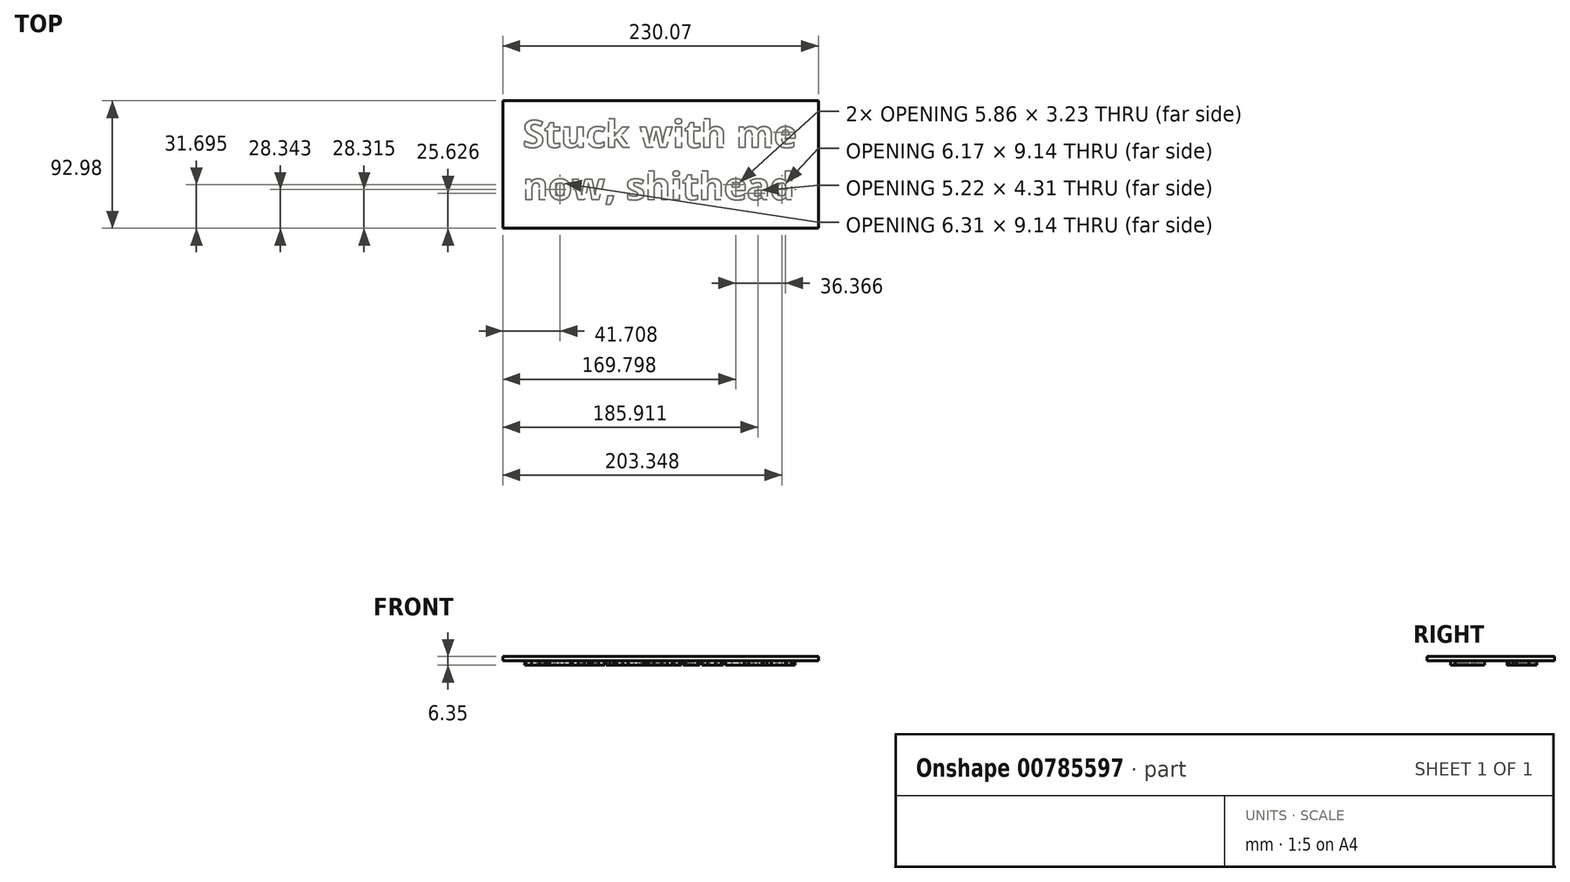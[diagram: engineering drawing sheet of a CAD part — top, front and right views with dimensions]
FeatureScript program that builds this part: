
annotation { "Feature Type Name" : "Feature", "Feature Type Description" : "" }
export const myFeature = defineFeature(function(context is Context, id is Id, definition is map)
    precondition{}
    {
        {
            var Q0;
            Q0=qCreatedBy(makeId("Top.planeOp"),FACE);
            var sketch = newSketch(context, id + "F0", { "sketchPlane" : qUnion([Q0])});
            skText(sketch, "E0", { "text": "Stuck with me\nnow, shithead", "fontName": "OpenSans-Bold.ttf"});
            const initialGuessF0  = {"E0": [0, 0, 1, 0, 0.02018]};
            skSetInitialGuess(sketch, initialGuessF0);
            skSolve(sketch);
        }
        {
            var Q0;
            Q0 = qSketchRegion(id + "F0", true);
            extrude(context, id + "F1", {"entities" : qUnion([Q0]), "depth" : 3.17 * mm, "offsetDistance" : 25.4 * mm});
        }
        {
            var Q0;
            Q0=makeQuery(id+"F1.opExtrude","CAP_FACE",FACE,{"disambiguationData":[OSD([sQuery(id+"F0.wireOp",EDGE,"E0.sketch_text.stroke-0"),sQuery(id+"F0.wireOp",EDGE,"E0.sketch_text.stroke-1"),sQuery(id+"F0.wireOp",EDGE,"E0.sketch_text.stroke-2"),sQuery(id+"F0.wireOp",EDGE,"E0.sketch_text.stroke-3"),sQuery(id+"F0.wireOp",EDGE,"E0.sketch_text.stroke-4"),sQuery(id+"F0.wireOp",EDGE,"E0.sketch_text.stroke-5"),sQuery(id+"F0.wireOp",EDGE,"E0.sketch_text.stroke-6"),sQuery(id+"F0.wireOp",EDGE,"E0.sketch_text.stroke-7"),sQuery(id+"F0.wireOp",EDGE,"E0.sketch_text.stroke-8"),sQuery(id+"F0.wireOp",EDGE,"E0.sketch_text.stroke-9"),sQuery(id+"F0.wireOp",EDGE,"E0.sketch_text.stroke-10"),sQuery(id+"F0.wireOp",EDGE,"E0.sketch_text.stroke-11"),sQuery(id+"F0.wireOp",EDGE,"E0.sketch_text.stroke-12"),sQuery(id+"F0.wireOp",EDGE,"E0.sketch_text.stroke-13"),sQuery(id+"F0.wireOp",EDGE,"E0.sketch_text.stroke-14"),sQuery(id+"F0.wireOp",EDGE,"E0.sketch_text.stroke-15"),sQuery(id+"F0.wireOp",EDGE,"E0.sketch_text.stroke-16"),sQuery(id+"F0.wireOp",EDGE,"E0.sketch_text.stroke-17"),sQuery(id+"F0.wireOp",EDGE,"E0.sketch_text.stroke-18"),sQuery(id+"F0.wireOp",EDGE,"E0.sketch_text.stroke-19"),sQuery(id+"F0.wireOp",EDGE,"E0.sketch_text.stroke-20"),sQuery(id+"F0.wireOp",EDGE,"E0.sketch_text.stroke-21"),sQuery(id+"F0.wireOp",EDGE,"E0.sketch_text.stroke-22"),sQuery(id+"F0.wireOp",EDGE,"E0.sketch_text.stroke-23"),sQuery(id+"F0.wireOp",EDGE,"E0.sketch_text.stroke-24"),sQuery(id+"F0.wireOp",EDGE,"E0.sketch_text.stroke-25"),sQuery(id+"F0.wireOp",EDGE,"E0.sketch_text.stroke-26"),sQuery(id+"F0.wireOp",EDGE,"E0.sketch_text.stroke-27")])],"isStart":false});
            var sketch = newSketch(context, id + "F2", { "sketchPlane" : qUnion([Q0])});
            skLineSegment(sketch, "E1.bottom", {"start": v(-14.62, 34.17) * mm, "end": v(215.45, 34.17) * mm});
            skLineSegment(sketch, "E1.top", {"start": v(-14.62, -58.81) * mm, "end": v(215.45, -58.81) * mm});
            skLineSegment(sketch, "E1.left", {"start": v(-14.62, 34.17) * mm, "end": v(-14.62, -58.81) * mm});
            skLineSegment(sketch, "E1.right", {"start": v(215.45, 34.17) * mm, "end": v(215.45, -58.81) * mm});
            skSolve(sketch);
        }
        {
            var Q0;
            Q0 = qSketchRegion(id + "F2", true);
            extrude(context, id + "F3", {"entities" : qUnion([Q0]), "depth" : 3.17 * mm, "offsetDistance" : 25.4 * mm});
        }
    });
